# Revit family: AL120
name_source: partatom
category: Двери
revit_build: Autodesk Revit 2016 (Build: 20150714_1515(x64)
units: mm (PartAtom-declared; Revit-internal decimal feet)

## family parameters
Всегда вертикально = Да
Заголовок OmniClass = Doors
Номер OmniClass = 23.30.10.00
Общий = Нет
Основа = Стена
При загрузке вырезать с полостями = Нет
Точка расчета площади = Нет

## types (1)
- AL-120
    ADSK_URL страницы изделия = https://www.fire-tec.ru
    ADSK_Завод-изготовитель = Firetechnics
    ADSK_Наименование = Рулонные противопожарные ворота FireTechnics-S EI60 с миниральным заполнителем
    ADSK_Предел огнестойкости = EI120
    ADSK_Размер_Высота = 3000 мм
    ADSK_Размер_Ширина = 3000 мм
    BL_ВысотаКороба = 297 мм
    BL_ДлинаНаправляющей = 60 мм
    BL_КоличествоФаз = 1
    BL_МатериалНаправляющих = BL_Сталь_Оцинкованная_Листовая_2мм_Firetechnics
    BL_МатериалПолотна = BL_АлюминийсДвойнойСтенкой_ВнутреннимНаполнениемизЖесткогоППУ_ПорошковойПокраскойпоRALs_Firetechnics
    BL_Напряжение = 220 В
    BL_ОтстаяниеотДвигателя = 130 мм
    BL_РазмерШага = 0 мм
    BL_ШиринаBходавПолотна = 40 мм
    BL_ШиринаВерхнейНаправляющей = 374 мм
    BL_ШиринаНаправляющих = 115 мм
    BL_ШиринаПолотна = 75 мм
    URL = https://www.fire-tec.ru
    Аналитическая конструкция = <Нет>
    Высота = 3000 мм
    Замыкание стены = По основе
    Изготовитель = Firetechnics
    Огнестойкость = AL120
    Функция = Внутренние слои
    Ширина = 3000 мм
    Штора открыто/закрыто = Да

## geometry (parser evidence)
native form markers: Blend x2
no freeform markers — native parametric forms only
